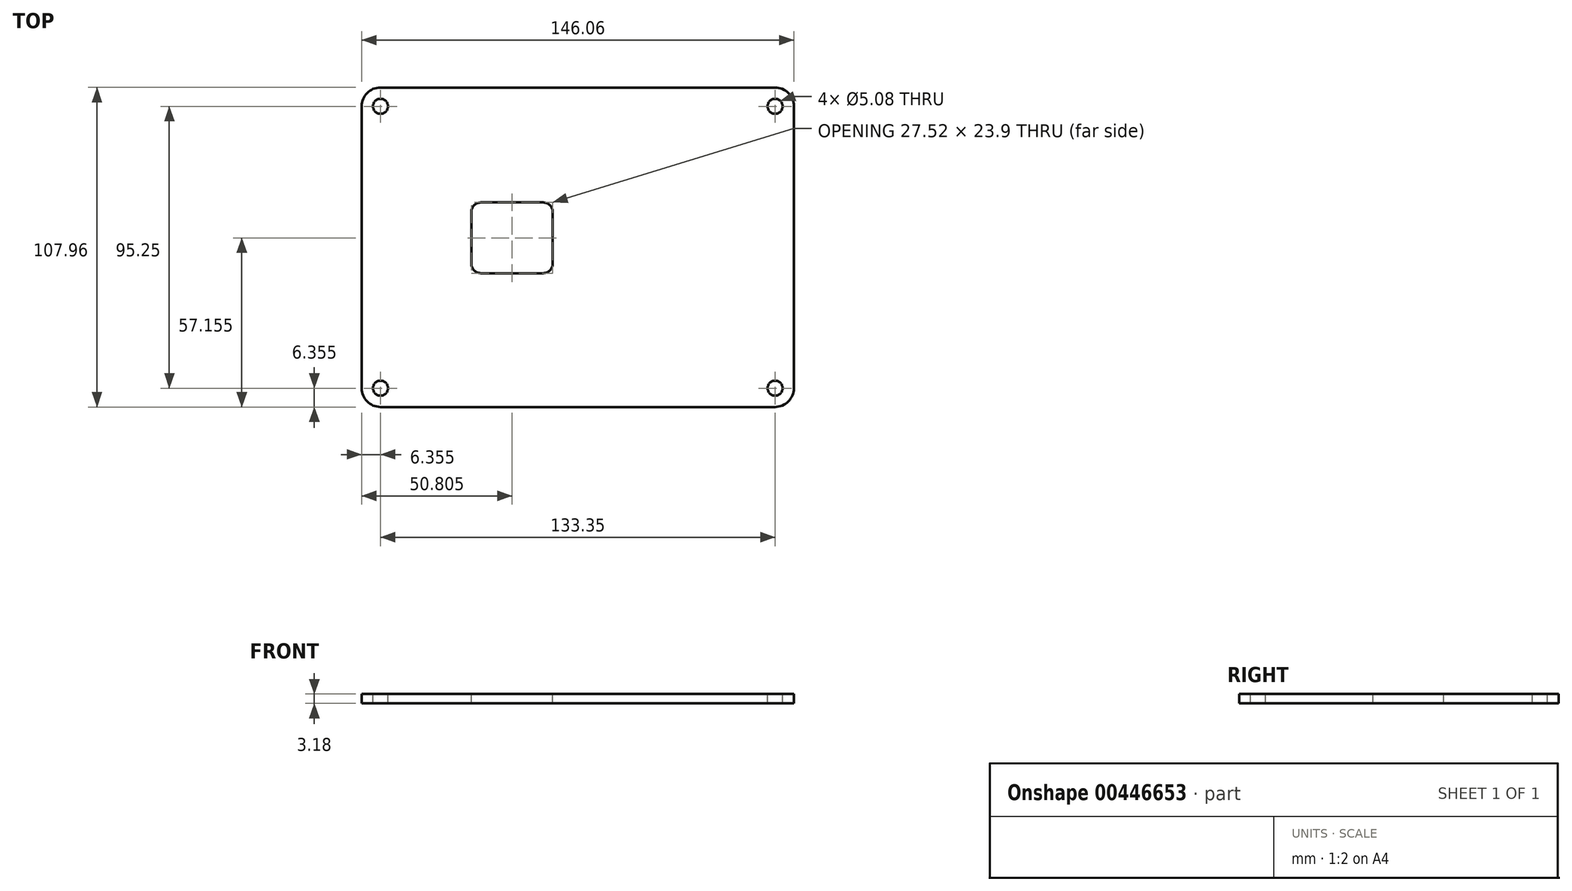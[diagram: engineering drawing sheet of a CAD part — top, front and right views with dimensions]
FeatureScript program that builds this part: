
annotation { "Feature Type Name" : "Feature", "Feature Type Description" : "" }
export const myFeature = defineFeature(function(context is Context, id is Id, definition is map)
    precondition{}
    {
        {
            var Q0;
            Q0=qCreatedBy(makeId("Top.planeOp"),FACE);
            var sketch = newSketch(context, id + "F0", { "sketchPlane" : qUnion([Q0])});
            skLineSegment(sketch, "E0.bottom", {"start": v(66.68, 53.98) * mm, "end": v(-66.67, 53.98) * mm});
            skLineSegment(sketch, "E0.top", {"start": v(66.67, -53.98) * mm, "end": v(-66.67, -53.98) * mm});
            skLineSegment(sketch, "E0.left", {"start": v(73.03, 47.63) * mm, "end": v(73.02, -47.63) * mm});
            skLineSegment(sketch, "E0.right", {"start": v(-73.02, 47.63) * mm, "end": v(-73.03, -47.63) * mm});
            skPoint(sketch, "E0.middle", {"position": v(0, 0) * mm});
            skPoint(sketch, "E1.visualSharp", {"position": v(-73.03, -53.98) * mm});
            skArc(sketch, "E1.filletArc", {"start": v(-73.03, -47.63) * mm, "mid": v(-71.17, -52.12) * mm, "end": v(-66.67, -53.98) * mm});
            skPoint(sketch, "E2.visualSharp", {"position": v(-73.02, 53.98) * mm});
            skArc(sketch, "E2.filletArc", {"start": v(-66.67, 53.98) * mm, "mid": v(-71.17, 52.12) * mm, "end": v(-73.02, 47.63) * mm});
            skPoint(sketch, "E3.visualSharp", {"position": v(73.02, -53.98) * mm});
            skArc(sketch, "E3.filletArc", {"start": v(66.67, -53.98) * mm, "mid": v(71.17, -52.12) * mm, "end": v(73.02, -47.63) * mm});
            skPoint(sketch, "E4.visualSharp", {"position": v(73.03, 53.98) * mm});
            skArc(sketch, "E4.filletArc", {"start": v(73.03, 47.63) * mm, "mid": v(71.17, 52.12) * mm, "end": v(66.68, 53.98) * mm});
            skSolve(sketch);
        }
        {
            var Q0;
            Q0 = qSketchRegion(id + "F0", true);
            extrude(context, id + "F1", {"entities" : qUnion([Q0]), "depth" : 3.17 * mm});
        }
        {
            var Q0;
            Q0=makeQuery(id+"F1.opExtrude","CAP_FACE",FACE,{"disambiguationData":[OSD([sQuery(id+"F0.wireOp",EDGE,"E0.bottom"),sQuery(id+"F0.wireOp",EDGE,"E0.top"),sQuery(id+"F0.wireOp",EDGE,"E0.left"),sQuery(id+"F0.wireOp",EDGE,"E0.right"),sQuery(id+"F0.wireOp",EDGE,"E1.filletArc"),sQuery(id+"F0.wireOp",EDGE,"E2.filletArc"),sQuery(id+"F0.wireOp",EDGE,"E3.filletArc"),sQuery(id+"F0.wireOp",EDGE,"E4.filletArc")])],"isStart":false});
            var sketch = newSketch(context, id + "F2", { "sketchPlane" : qUnion([Q0])});
            skLineSegment(sketch, "E5.bottom", {"start": v(66.68, -47.62) * mm, "end": v(-66.68, -47.63) * mm});
            skLineSegment(sketch, "E5.top", {"start": v(66.67, 47.63) * mm, "end": v(-66.68, 47.63) * mm});
            skLineSegment(sketch, "E5.left", {"start": v(66.68, -47.62) * mm, "end": v(66.67, 47.63) * mm});
            skLineSegment(sketch, "E5.right", {"start": v(-66.67, -47.63) * mm, "end": v(-66.68, 47.63) * mm});
            skPoint(sketch, "E5.middle", {"position": v(0, 0) * mm});
            skSolve(sketch);
        }
        {
            var Q0;
            Q0=sQuery(id+"F2.wireOp",VERTEX,"E5.top.end");
            var Q1;
            Q1=sQuery(id+"F2.wireOp",VERTEX,"E5.left.end");
            var Q2;
            Q2=sQuery(id+"F2.wireOp",VERTEX,"E5.left.start");
            var Q3;
            Q3=sQuery(id+"F2.wireOp",VERTEX,"E5.right.start");
            var Q4;
            Q4=makeQuery(id+"F1.opExtrude","SWEPT_BODY",BODY,{"disambiguationData":[OSD([sQuery(id+"F0.wireOp",EDGE,"E0.bottom"),sQuery(id+"F0.wireOp",EDGE,"E0.top"),sQuery(id+"F0.wireOp",EDGE,"E0.left"),sQuery(id+"F0.wireOp",EDGE,"E0.right"),sQuery(id+"F0.wireOp",EDGE,"E1.filletArc"),sQuery(id+"F0.wireOp",EDGE,"E2.filletArc"),sQuery(id+"F0.wireOp",EDGE,"E3.filletArc"),sQuery(id+"F0.wireOp",EDGE,"E4.filletArc")])]});
            hole(context, id + "F3", {"style" : HoleStyle.SIMPLE, "endStyle" : HoleEndStyle.THROUGH, "holeDiameter" : 5.08 * mm, "isTappedThrough" : true, "tappedDepth" : 12.7 * mm, "tapClearance" : 3, "startFromSketch" : true, "locations" : qUnion([Q0, Q1, Q2, Q3]), "scope" : qUnion([Q4])});
        }
        {
            var Q0;
            Q0=makeQuery(id+"F1.opExtrude","CAP_FACE",FACE,{"disambiguationData":[OSD([sQuery(id+"F0.wireOp",EDGE,"E0.bottom"),sQuery(id+"F0.wireOp",EDGE,"E0.top"),sQuery(id+"F0.wireOp",EDGE,"E0.left"),sQuery(id+"F0.wireOp",EDGE,"E0.right"),sQuery(id+"F0.wireOp",EDGE,"E1.filletArc"),sQuery(id+"F0.wireOp",EDGE,"E2.filletArc"),sQuery(id+"F0.wireOp",EDGE,"E3.filletArc"),sQuery(id+"F0.wireOp",EDGE,"E4.filletArc")])],"isStart":false});
            var sketch = newSketch(context, id + "F4", { "sketchPlane" : qUnion([Q0])});
            skLineSegment(sketch, "E6.bottom", {"start": v(-11.64, -8.78) * mm, "end": v(-32.81, -8.78) * mm});
            skLineSegment(sketch, "E6.top", {"start": v(-11.64, 15.13) * mm, "end": v(-32.81, 15.13) * mm});
            skLineSegment(sketch, "E6.left", {"start": v(-8.46, -5.6) * mm, "end": v(-8.46, 11.95) * mm});
            skLineSegment(sketch, "E6.right", {"start": v(-35.99, -5.6) * mm, "end": v(-35.99, 11.95) * mm});
            skPoint(sketch, "E6.middle", {"position": v(-22.22, 3.18) * mm});
            skPoint(sketch, "E7.visualSharp", {"position": v(-35.99, 15.13) * mm});
            skArc(sketch, "E7.filletArc", {"start": v(-32.81, 15.13) * mm, "mid": v(-35.06, 14.2) * mm, "end": v(-35.99, 11.95) * mm});
            skPoint(sketch, "E8.visualSharp", {"position": v(-35.99, -8.78) * mm});
            skArc(sketch, "E8.filletArc", {"start": v(-35.99, -5.6) * mm, "mid": v(-35.06, -7.85) * mm, "end": v(-32.81, -8.78) * mm});
            skPoint(sketch, "E9.visualSharp", {"position": v(-8.46, -8.78) * mm});
            skArc(sketch, "E9.filletArc", {"start": v(-11.64, -8.78) * mm, "mid": v(-9.4, -7.85) * mm, "end": v(-8.46, -5.6) * mm});
            skPoint(sketch, "E10.visualSharp", {"position": v(-8.46, 15.13) * mm});
            skArc(sketch, "E10.filletArc", {"start": v(-8.46, 11.95) * mm, "mid": v(-9.4, 14.2) * mm, "end": v(-11.64, 15.13) * mm});
            skSolve(sketch);
        }
        {
            var Q0;
            Q0 = qSketchRegion(id + "F4", true);
            extrude(context, id + "F5", {"entities" : qUnion([Q0]), "operationType" : NewBodyOperationType.REMOVE, "endBound" : BoundingType.THROUGH_ALL, "oppositeDirection" : true, "depth" : 25.4 * mm});
        }
    });
